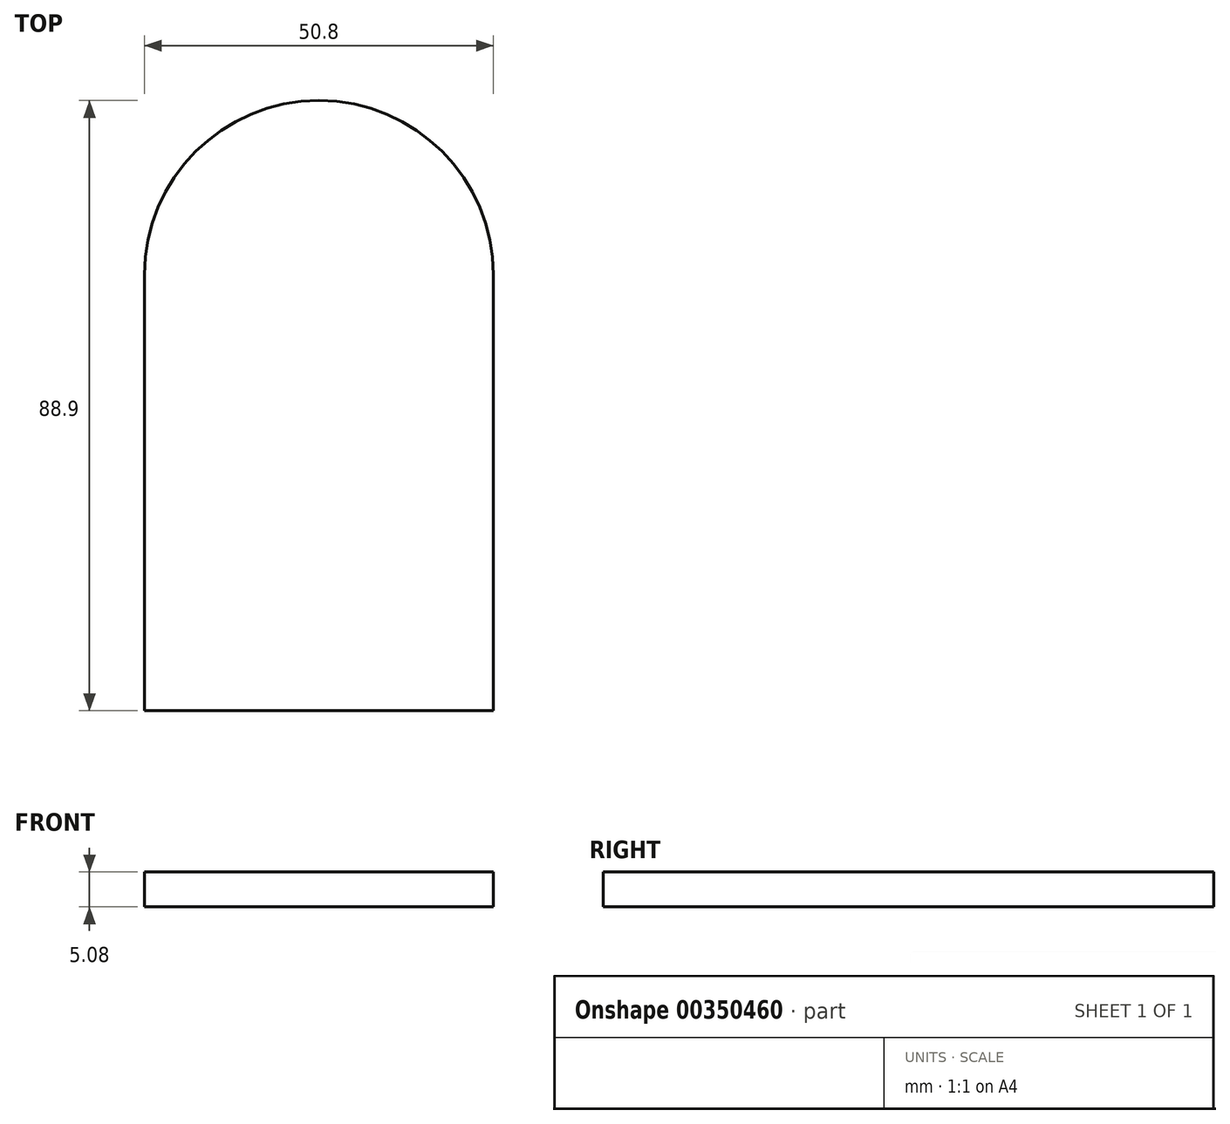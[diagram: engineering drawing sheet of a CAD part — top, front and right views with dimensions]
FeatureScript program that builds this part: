
annotation { "Feature Type Name" : "Feature", "Feature Type Description" : "" }
export const myFeature = defineFeature(function(context is Context, id is Id, definition is map)
    precondition{}
    {
        {
            var Q0;
            Q0=qCreatedBy(makeId("Top.planeOp"),FACE);
            var sketch = newSketch(context, id + "F0", { "sketchPlane" : qUnion([Q0])});
            skLineSegment(sketch, "E0", {"start": v(-25.4, 0) * mm, "end": v(25.4, 0) * mm});
            skLineSegment(sketch, "E1", {"start": v(25.4, 0) * mm, "end": v(25.4, 63.5) * mm});
            skLineSegment(sketch, "E2", {"start": v(-25.4, 0) * mm, "end": v(-25.4, 63.5) * mm});
            skArc(sketch, "E3", {"start": v(25.4, 63.5) * mm, "mid": v(0, 88.9) * mm, "end": v(-25.4, 63.5) * mm});
            skPoint(sketch, "E4.secondSnap0", {"position": v(6.86, 66.04) * mm});
            skSolve(sketch);
        }
        {
            var Q0;
            Q0 = qSketchRegion(id + "F0", true);
            extrude(context, id + "F1", {"entities" : qUnion([Q0]), "depth" : 5.08 * mm});
        }
    });
